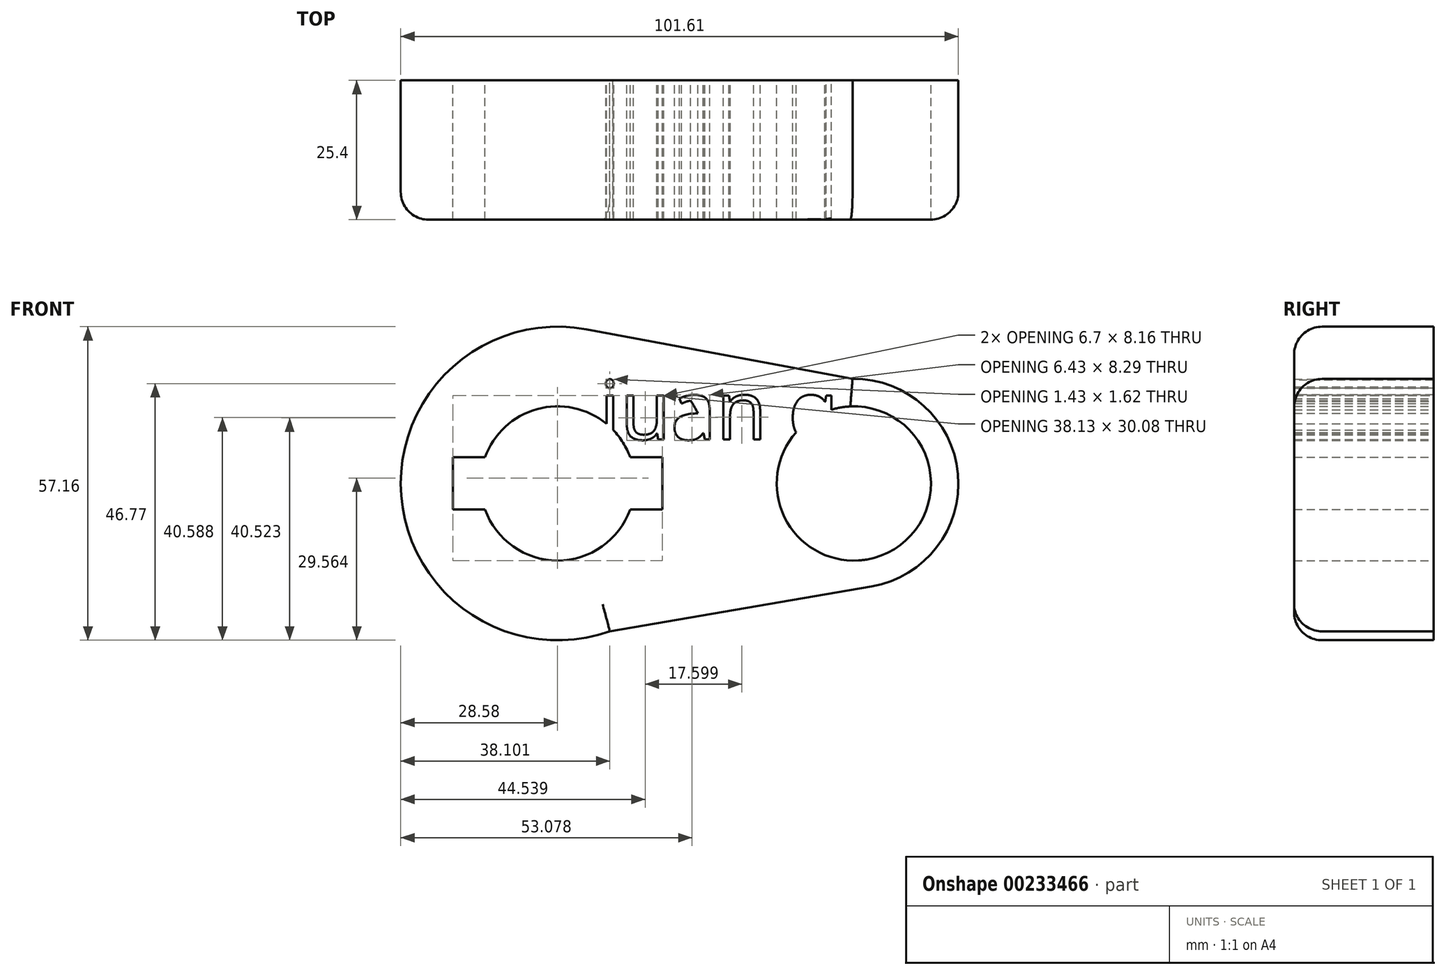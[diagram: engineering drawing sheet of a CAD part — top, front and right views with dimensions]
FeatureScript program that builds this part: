
annotation { "Feature Type Name" : "Feature", "Feature Type Description" : "" }
export const myFeature = defineFeature(function(context is Context, id is Id, definition is map)
    precondition{}
    {
        {
            var Q0;
            Q0=qCreatedBy(makeId("Front.planeOp"),FACE);
            var sketch = newSketch(context, id + "F0", { "sketchPlane" : qUnion([Q0])});
            skCircle(sketch, "E0", {"center": v(0, 0) * mm, "radius": 28.58 * mm});
            skCircle(sketch, "E1", {"center": v(53.98, 0) * mm, "radius": 19.05 * mm});
            skLineSegment(sketch, "E2", {"start": v(5.24, 28.1) * mm, "end": v(53.74, 19.05) * mm});
            skLineSegment(sketch, "E3", {"start": v(0, -28.58) * mm, "end": v(57.2, -18.78) * mm});
            skCircle(sketch, "E4", {"center": v(0, 0) * mm, "radius": 14.06 * mm});
            skCircle(sketch, "E5", {"center": v(53.98, 0) * mm, "radius": 14.06 * mm});
            skLineSegment(sketch, "E6.bottom", {"start": v(19.06, -4.76) * mm, "end": v(-19.06, -4.76) * mm});
            skLineSegment(sketch, "E6.top", {"start": v(19.06, 4.76) * mm, "end": v(-19.06, 4.76) * mm});
            skLineSegment(sketch, "E6.left", {"start": v(19.06, -4.76) * mm, "end": v(19.06, 4.76) * mm});
            skLineSegment(sketch, "E6.right", {"start": v(-19.06, -4.76) * mm, "end": v(-19.06, 4.76) * mm});
            skText(sketch, "E7", { "text": "juan q", "fontName": "OpenSans-Regular.ttf"});
            const initialGuessF0  = {"E7": [0.00762, 0.00801, 1, 0, 0.01078]};
            skSetInitialGuess(sketch, initialGuessF0);
            skSolve(sketch);
        }
        {
            var Q0;
            Q0 = qSketchRegion(id + "F0", true);
            extrude(context, id + "F1", {"entities" : qUnion([Q0]), "depth" : 25.4 * mm});
        }
        {
            var Q0;
            Q0=makeQuery(id+"F1.opExtrude","CAP_EDGE",EDGE,{"disambiguationData":[OSD([sQuery(id+"F0.wireOp",EDGE,"E2")])],"isStart":false});
            var Q1;
            Q1=makeQuery(id+"F1.opExtrude","CAP_EDGE",EDGE,{"disambiguationData":[OSD([sQuery(id+"F0.wireOp",EDGE,"E1")])],"isStart":false});
            var Q2;
            Q2=makeQuery(id+"F1.opExtrude","CAP_EDGE",EDGE,{"disambiguationData":[OSD([sQuery(id+"F0.wireOp",EDGE,"E3")])],"isStart":false});
            fillet(context, id + "F2", {"entities" : qUnion([Q0, Q1, Q2]), "radius" : 5.08 * mm, "tangentPropagation" : true, "allowEdgeOverflow" : false});
        }
    });
